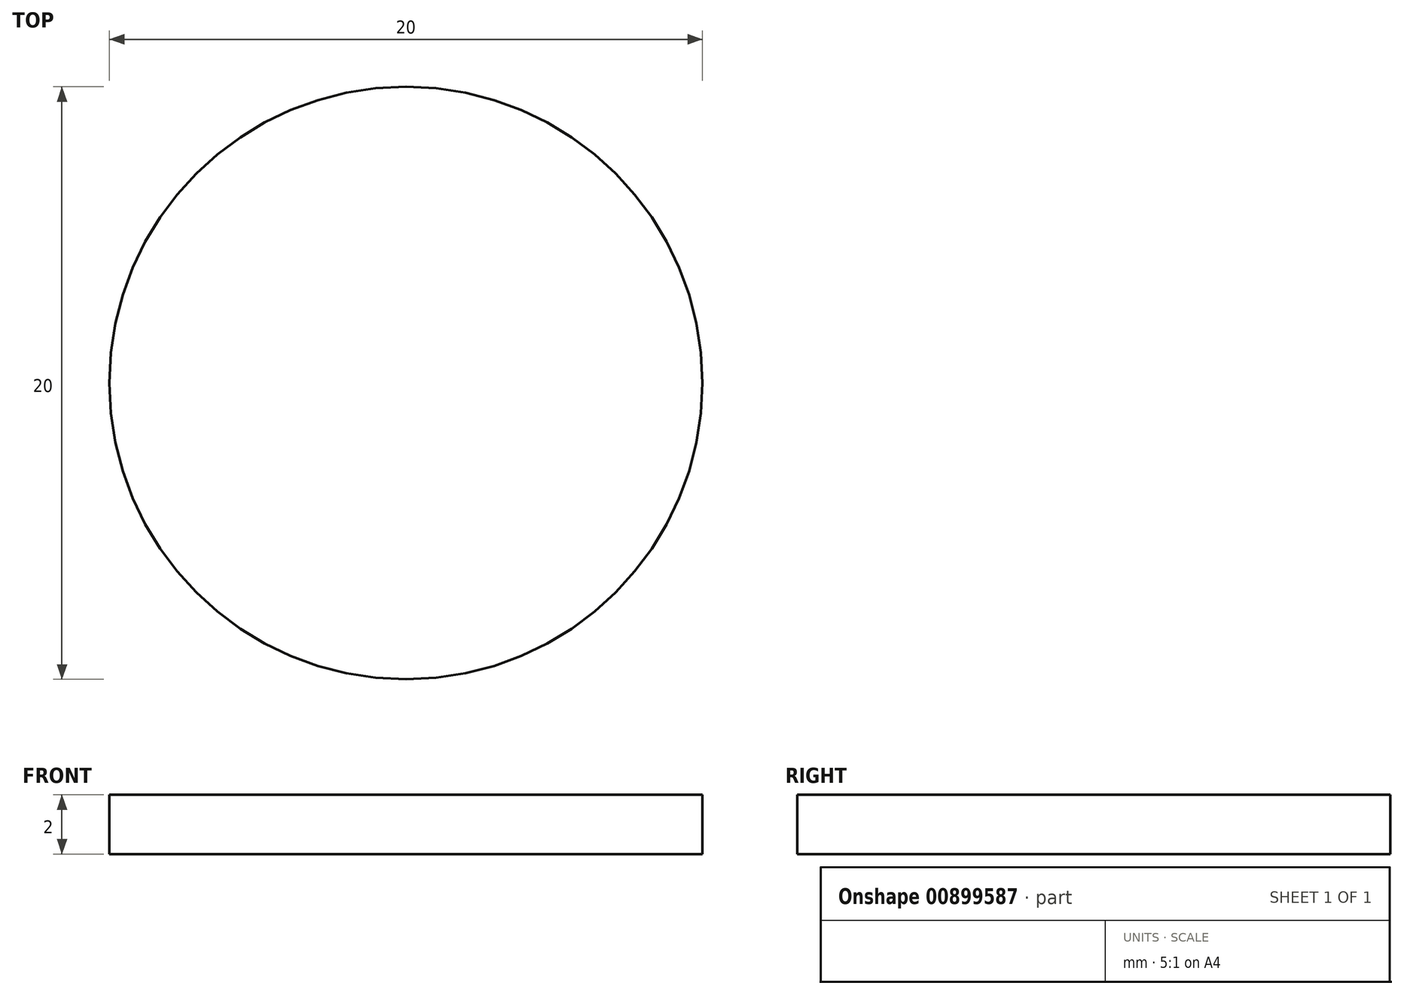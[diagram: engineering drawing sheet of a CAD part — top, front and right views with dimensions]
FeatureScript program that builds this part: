
annotation { "Feature Type Name" : "Feature", "Feature Type Description" : "" }
export const myFeature = defineFeature(function(context is Context, id is Id, definition is map)
    precondition{}
    {
        {
            var Q0;
            Q0=qCreatedBy(makeId("Top.planeOp"),FACE);
            var sketch = newSketch(context, id + "F0", { "sketchPlane" : qUnion([Q0])});
            skCircle(sketch, "E0", {"center": v(0, 0) * mm, "radius": 10 * mm});
            skSolve(sketch);
        }
        {
            var Q0;
            Q0=makeQuery(id+"F0.imprint","IMPRINT",FACE,{"disambiguationData":[TD([[makeQuery(id+"F0.imprint","IMPRINT",EDGE,{"derivedFrom":sQuery(id+"F0.wireOp",EDGE,"E0")}),1.0]])]});
            extrude(context, id + "F1", {"entities" : qUnion([Q0]), "depth" : 2 * mm, "offsetDistance" : 25 * mm});
        }
    });
